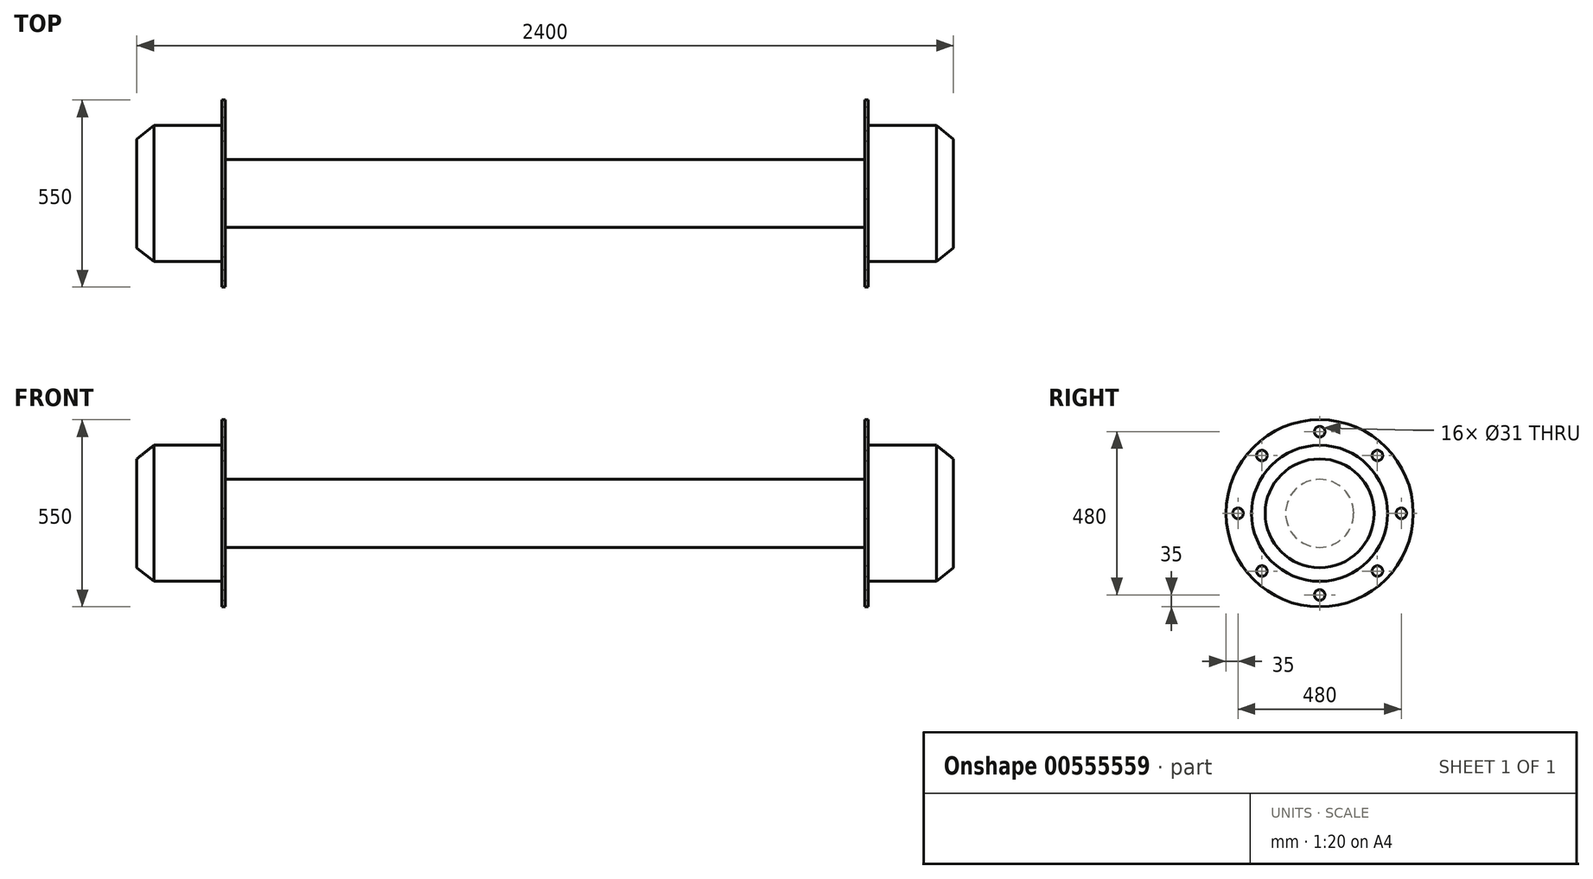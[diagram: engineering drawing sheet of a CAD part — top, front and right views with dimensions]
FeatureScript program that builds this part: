
annotation { "Feature Type Name" : "Feature", "Feature Type Description" : "" }
export const myFeature = defineFeature(function(context is Context, id is Id, definition is map)
    precondition{}
    {
        {
            var Q0;
            Q0=qCreatedBy(makeId("Front.planeOp"),FACE);
            var sketch = newSketch(context, id + "F0", { "sketchPlane" : qUnion([Q0])});
            skLineSegment(sketch, "E0", {"start": v(-1359.48, 0) * mm, "end": v(1359.48, 0) * mm, "construction": true});
            skLineSegment(sketch, "E1", {"start": v(-940, 100) * mm, "end": v(940, 100) * mm});
            skLineSegment(sketch, "E2", {"start": v(950, 200) * mm, "end": v(1150, 200) * mm});
            skLineSegment(sketch, "E3", {"start": v(1150, 200) * mm, "end": v(1200, 160) * mm});
            skLineSegment(sketch, "E4", {"start": v(1200, 160) * mm, "end": v(1200, 0) * mm});
            skLineSegment(sketch, "E5", {"start": v(-950, 200) * mm, "end": v(-1150, 200) * mm});
            skLineSegment(sketch, "E6", {"start": v(-1150, 200) * mm, "end": v(-1200, 160) * mm});
            skLineSegment(sketch, "E7", {"start": v(-1200, 160) * mm, "end": v(-1200, 0) * mm});
            skLineSegment(sketch, "E8", {"start": v(-950, 200) * mm, "end": v(-950, 275) * mm});
            skLineSegment(sketch, "E9", {"start": v(-950, 275) * mm, "end": v(-940, 275) * mm});
            skLineSegment(sketch, "E10", {"start": v(-940, 275) * mm, "end": v(-940, 100) * mm});
            skLineSegment(sketch, "E11", {"start": v(950, 200) * mm, "end": v(950, 275) * mm});
            skLineSegment(sketch, "E12", {"start": v(950, 275) * mm, "end": v(940, 275) * mm});
            skLineSegment(sketch, "E13", {"start": v(940, 275) * mm, "end": v(940, 100) * mm});
            skLineSegment(sketch, "E14", {"start": v(-1200, 0) * mm, "end": v(1200, 0) * mm});
            skSolve(sketch);
        }
        {
            var Q0;
            Q0 = qSketchRegion(id + "F0", true);
            var Q1;
            Q1=sQuery(id+"F0.wireOp",EDGE,"E0");
            revolve(context, id + "F1", {"surfaceOperationType" : NewSurfaceOperationType.NEW, "entities" : qUnion([Q0]), "axis" : qUnion([Q1]), "revolveType" : RevolveType.FULL});
        }
        {
            var Q0;
            Q0=makeQuery(id+"F1.opRevolve","SWEPT_FACE",FACE,{"disambiguationData":[OSD([sQuery(id+"F0.wireOp",EDGE,"E11")])]});
            var sketch = newSketch(context, id + "F2", { "sketchPlane" : qUnion([Q0])});
            skCircle(sketch, "E15", {"center": v(0, 240) * mm, "radius": 15.5 * mm});
            skCircle(sketch, "E16.1.0", {"center": v(-169.7, 169.7) * mm, "radius": 15.5 * mm});
            skCircle(sketch, "E16.2.0", {"center": v(-240, 0) * mm, "radius": 15.5 * mm});
            skCircle(sketch, "E16.3.0", {"center": v(-169.7, -169.7) * mm, "radius": 15.5 * mm});
            skCircle(sketch, "E16.4.0", {"center": v(0, -240) * mm, "radius": 15.5 * mm});
            skCircle(sketch, "E16.5.0", {"center": v(169.7, -169.7) * mm, "radius": 15.5 * mm});
            skCircle(sketch, "E16.6.0", {"center": v(240, 0) * mm, "radius": 15.5 * mm});
            skCircle(sketch, "E16.7.0", {"center": v(169.7, 169.7) * mm, "radius": 15.5 * mm});
            skPoint(sketch, "E16.center", {"position": v(0, 0) * mm});
            skSolve(sketch);
        }
        {
            var Q0;
            Q0 = qSketchRegion(id + "F2", true);
            extrude(context, id + "F3", {"entities" : qUnion([Q0]), "operationType" : NewBodyOperationType.REMOVE, "endBound" : BoundingType.THROUGH_ALL, "oppositeDirection" : true, "depth" : 25 * mm, "offsetDistance" : 25 * mm});
        }
    });
